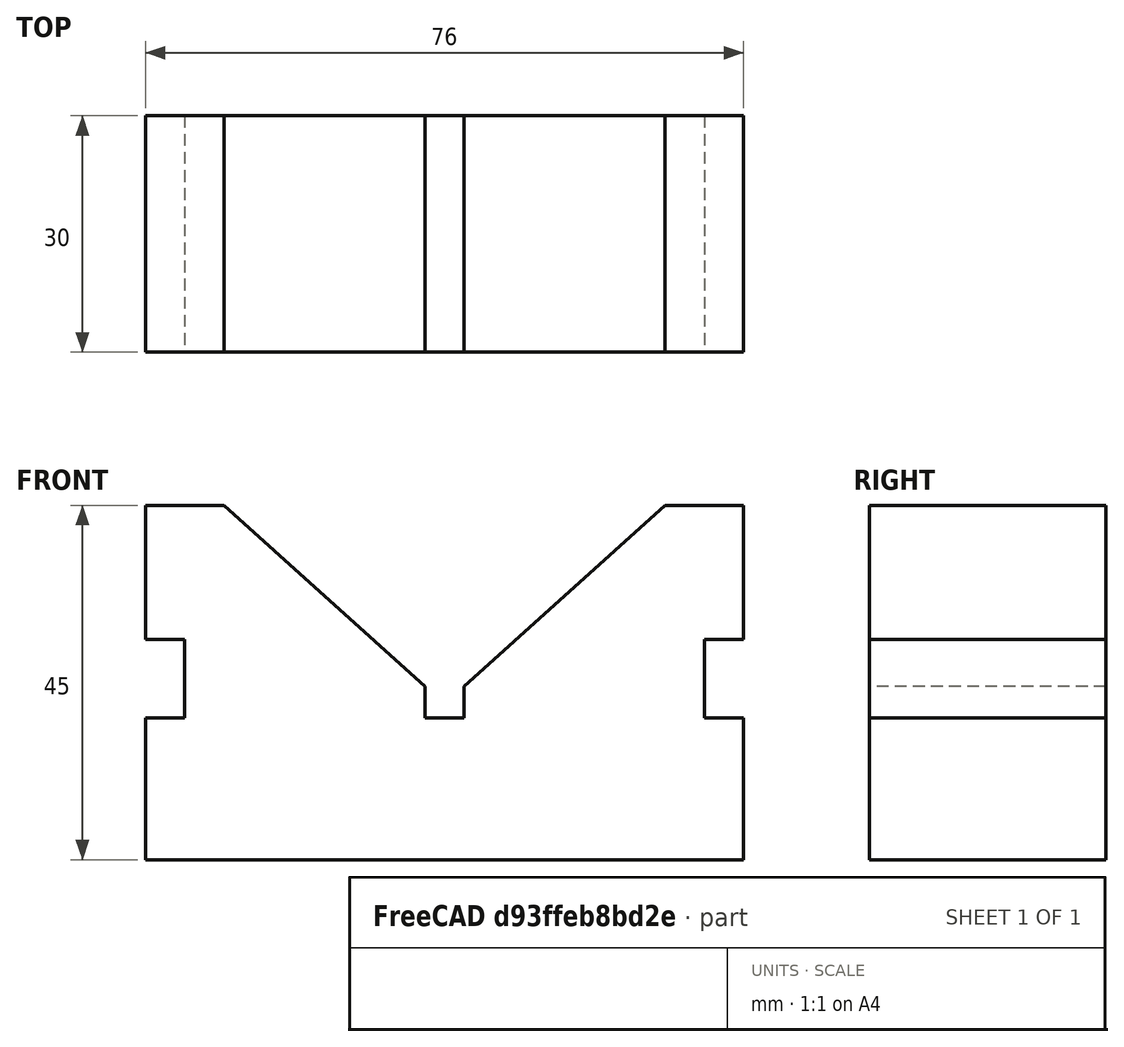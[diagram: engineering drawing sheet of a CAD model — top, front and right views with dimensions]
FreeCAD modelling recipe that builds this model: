
FCSTD DOCUMENT  (FreeCAD 0.18R4 (GitTag))
Label: Assignment-1
License: All rights reserved
LicenseURL: http://en.wikipedia.org/wiki/All_rights_reserved
objects: TechDraw::DrawViewDimension×9, TechDraw::DrawViewAnnotation×4, TechDraw::DrawViewPart×3, Sketcher::SketchObject×1, PartDesign::Pad×1, PartDesign::Body×1, TechDraw::DrawSVGTemplate×1, TechDraw::DrawPage×1
note: 4 computed .brp shape members not serialized (recipe doc carries the construction recipe); baked Part::Feature solids carry a one-line shape summary decoded from their .brp

FEATURE [Sketcher::SketchObject] Sketch
  MapMode = 5
  Placement = pos=(0,0,0) rot=(1,0,0;1.5708rad)
  Support = -> [XZ_Plane]
  sketch-geometry (20):
    g0: LineSegment StartX=0 StartY=0 StartZ=0 EndX=-38 EndY=0 EndZ=0
    g1: LineSegment StartX=-38 StartY=18 StartZ=0 EndX=-38 EndY=0 EndZ=0
    g2: LineSegment StartX=-38 StartY=18 StartZ=0 EndX=-33 EndY=18 EndZ=0
    g3: LineSegment StartX=-33 StartY=28 StartZ=0 EndX=-33 EndY=18 EndZ=0
    g4: LineSegment StartX=-38 StartY=28 StartZ=0 EndX=-33 EndY=28 EndZ=0
    g5: LineSegment StartX=-38 StartY=45 StartZ=0 EndX=-38 EndY=28 EndZ=0
    g6: LineSegment StartX=-38 StartY=45 StartZ=0 EndX=-28 EndY=45 EndZ=0
    g7: LineSegment StartX=-28 StartY=45 StartZ=0 EndX=-2.5 EndY=22 EndZ=0
    g8: LineSegment StartX=-2.5 StartY=22 StartZ=0 EndX=-2.5 EndY=18 EndZ=0
    g9: LineSegment StartX=-2.5 StartY=18 StartZ=0 EndX=0 EndY=18 EndZ=0
    g10: LineSegment StartX=0 StartY=0 StartZ=0 EndX=38 EndY=0 EndZ=0
    g11: LineSegment StartX=38 StartY=18 StartZ=0 EndX=38 EndY=0 EndZ=0
    g12: LineSegment StartX=38 StartY=18 StartZ=0 EndX=33 EndY=18 EndZ=0
    g13: LineSegment StartX=33 StartY=28 StartZ=0 EndX=33 EndY=18 EndZ=0
    g14: LineSegment StartX=38 StartY=28 StartZ=0 EndX=33 EndY=28 EndZ=0
    g15: LineSegment StartX=38 StartY=45 StartZ=0 EndX=38 EndY=28 EndZ=0
    g16: LineSegment StartX=38 StartY=45 StartZ=0 EndX=28 EndY=45 EndZ=0
    g17: LineSegment StartX=28 StartY=45 StartZ=0 EndX=2.5 EndY=22 EndZ=0
    g18: LineSegment StartX=2.5 StartY=22 StartZ=0 EndX=2.5 EndY=18 EndZ=0
    g19: LineSegment StartX=2.5 StartY=18 StartZ=0 EndX=0 EndY=18 EndZ=0
  constraints (56):
    c: Coincident(g0,g-1)
    c: Parallel(g0,g-1)
    c: DistanceX(g0,g0) = 38
    c: Coincident(g1,g0)
    c: Parallel(g1,g-2)
    c: DistanceY(g1,g1) = 18
    c: Coincident(g2,g1)
    c: Parallel(g2,g-1)
    c: DistanceX(g2,g2) = 5
    c: Coincident(g3,g2)
    c: Parallel(g3,g-2)
    c: DistanceY(g3,g3) = 10
    c: Coincident(g3,g4)
    c: Parallel(g-1,g4)
    c: DistanceX(g4,g4) = 5
    c: Coincident(g5,g4)
    c: Parallel(g5,g-2)
    c: DistanceY(g5,g5) = 17
    c: Coincident(g6,g5)
    c: Parallel(g6,g-1)
    c: DistanceX(g6,g6) = 10
    c: DistanceY(g0,g7) = 22
    c: Coincident(g7,g6)
    c: Coincident(g8,g7)
    c: Parallel(g8,g-2)
    c: DistanceY(g8,g8) = 4
    c: Coincident(g9,g8)
    c: Parallel(g9,g0)
    c: DistanceX(g9,g9) = 2.5
    c: Coincident(g11,g10)
    c: Coincident(g12,g11)
    c: Coincident(g13,g12)
    c: Coincident(g13,g14)
    c: Coincident(g15,g14)
    c: Coincident(g16,g15)
    c: Coincident(g17,g16)
    c: Coincident(g18,g17)
    c: Coincident(g19,g18)
    c: Parallel(g19,g10)
    c: Equal(g7,g17)
    c: Equal(g16,g6)
    c: Equal(g15,g5)
    c: Equal(g9,g19)
    c: Equal(g8,g18)
    c: Equal(g5,g15)
    c: Equal(g4,g14)
    c: Equal(g3,g13)
    c: Equal(g2,g12)
    c: Equal(g1,g11)
    c: Equal(g0,g10)
    c: Equal(g1,g11)
    c: Equal(g16,g6)
    c: Equal(g18,g8)
    c: Equal(g6,g16)
    c: Equal(g6,g16)
    c: Equal(g9,g19)
FEATURE [PartDesign::Pad] Pad
  Length = 30
  Length2 = 100
  Placement = pos=(0,0,0) rot=(1,0,0;1.5708rad)
  Profile = -> Sketch
  Type = 0
FEATURE [PartDesign::Body] Body
  Group = -> [Sketch,Pad]
  Origin = -> Origin
  Tip = -> Pad
FEATURE [TechDraw::DrawSVGTemplate] Template
  EditableTexts = Designed_by_Name=SOUMOJIT SHOME; Drawing_number=Drawing number - 02; FC-Date=08/11/2022; FC-SC=1:1; FC-SH=02; FC-Title=Academy of Technology; Subtitle=ECE-3 (X) ROLL- 139; Weight=Weight
  Height = 210
  Orientation = 1
  Width = 297
FEATURE [TechDraw::DrawViewPart] View
  CoarseView = false
  Direction = (0,-1,0)
  Focus = 100
  HardHidden = false
  IsoCount = 0
  IsoHidden = false
  IsoVisible = false
  LockPosition = false
  Perspective = false
  Rotation = 0
  ScaleType = 0
  SeamHidden = false
  SeamVisible = false
  SmoothHidden = false
  SmoothVisible = false
  Source = -> [Pad]
  X = 81.9468
  Y = 154.318
FEATURE [TechDraw::DrawViewPart] View001
  CoarseView = false
  Direction = (0,0,1)
  Focus = 100
  HardHidden = false
  IsoCount = 0
  IsoHidden = false
  IsoVisible = false
  LockPosition = false
  Perspective = false
  Rotation = 0
  ScaleType = 0
  SeamHidden = false
  SeamVisible = false
  SmoothHidden = false
  SmoothVisible = false
  Source = -> [Pad]
  X = 79.6067
  Y = 63.498
FEATURE [TechDraw::DrawViewPart] View002
  CoarseView = false
  Direction = (0.577,-0.577,0.577)
  Focus = 100
  HardHidden = false
  IsoCount = 0
  IsoHidden = false
  IsoVisible = false
  LockPosition = false
  Perspective = false
  Rotation = 0
  ScaleType = 0
  SeamHidden = false
  SeamVisible = false
  SmoothHidden = false
  SmoothVisible = false
  Source = -> [Pad]
  X = 215.733
  Y = 138.202
FEATURE [TechDraw::DrawViewDimension] Dimension
  Arbitrary = false
  FormatSpec = %.2f
  LockPosition = false
  MeasureType = 1
  OverTolerance = 0
  References2D = -> [View]
  Rotation = 0
  ScaleType = 0
  Type = 1
  UnderTolerance = 0
  X = -37.1162
  Y = 35.9027
FEATURE [TechDraw::DrawViewDimension] Dimension001
  Arbitrary = false
  FormatSpec = %.2f
  LockPosition = false
  MeasureType = 1
  OverTolerance = 0
  References2D = -> [View]
  Rotation = 0
  ScaleType = 0
  Type = 2
  UnderTolerance = 0
  X = 50.4704
  Y = 6.63661
FEATURE [TechDraw::DrawViewDimension] Dimension002
  Arbitrary = false
  FormatSpec = %.2f
  LockPosition = false
  MeasureType = 1
  OverTolerance = 0
  References2D = -> [View]
  Rotation = 0
  ScaleType = 0
  Type = 1
  UnderTolerance = 0
  X = 12.5602
  Y = -40.9168
FEATURE [TechDraw::DrawViewDimension] Dimension003
  Arbitrary = false
  FormatSpec = %.2f
  LockPosition = false
  MeasureType = 1
  OverTolerance = 0
  References2D = -> [View]
  Rotation = 0
  ScaleType = 0
  Type = 2
  UnderTolerance = 0
  X = -59.0003
  Y = 10.7875
FEATURE [TechDraw::DrawViewDimension] Dimension004
  Arbitrary = false
  FormatSpec = %.2f
  LockPosition = false
  MeasureType = 1
  OverTolerance = 0
  References2D = -> [View]
  Rotation = 0
  ScaleType = 0
  Type = 2
  UnderTolerance = 0
  X = -66.4537
  Y = -19.373
FEATURE [TechDraw::DrawViewDimension] Dimension005
  Arbitrary = false
  FormatSpec = %.2f
  LockPosition = false
  MeasureType = 1
  OverTolerance = 0
  References2D = -> [View001]
  Rotation = 0
  ScaleType = 0
  Type = 2
  UnderTolerance = 0
  X = 51.9004
  Y = 5.42978
FEATURE [TechDraw::DrawViewDimension] Dimension006
  Arbitrary = false
  FormatSpec = %.2f
  LockPosition = false
  MeasureType = 1
  OverTolerance = 0
  References2D = -> [View]
  Rotation = 0
  ScaleType = 0
  Type = 2
  UnderTolerance = 0
  X = 9.18176
  Y = 26.9807
FEATURE [TechDraw::DrawViewDimension] Dimension007
  Arbitrary = false
  FormatSpec = %.2f
  LockPosition = false
  MeasureType = 1
  OverTolerance = 0
  References2D = -> [View]
  Rotation = 0
  ScaleType = 0
  Type = 1
  UnderTolerance = 0
  X = -24.0065
  Y = -29.8891
FEATURE [TechDraw::DrawViewDimension] Dimension008
  Arbitrary = false
  FormatSpec = %.2f
  LockPosition = false
  MeasureType = 1
  OverTolerance = 0
  References2D = -> [View]
  Rotation = 0
  ScaleType = 0
  Type = 1
  UnderTolerance = 0
  X = -7.80517
  Y = 25.714
FEATURE [TechDraw::DrawViewAnnotation] Annotation
  Font = osifont
  LineSpace = 80
  LockPosition = false
  MaxWidth = -1
  Rotation = 0
  ScaleType = 0
  Text = Front View
  TextSize = 5
  TextStyle = 0
  X = 79.4432
  Y = 100.619
FEATURE [TechDraw::DrawViewAnnotation] Annotation001
  Font = osifont
  LineSpace = 80
  LockPosition = false
  MaxWidth = -1
  Rotation = 0
  ScaleType = 0
  Text = Top View
  TextSize = 5
  TextStyle = 0
  X = 79.0418
  Y = 34.1008
FEATURE [TechDraw::DrawViewAnnotation] Annotation002
  Font = osifont
  LineSpace = 80
  LockPosition = false
  MaxWidth = -1
  Rotation = 0
  ScaleType = 0
  Text = Isometric View
  TextSize = 5
  TextStyle = 0
  X = 203.252
  Y = 86.2075
FEATURE [TechDraw::DrawViewAnnotation] Annotation003
  Font = osifont
  LineSpace = 80
  LockPosition = false
  MaxWidth = -1
  Rotation = 0
  ScaleType = 0
  Text =  V Block
  TextSize = 5
  TextStyle = 0
  X = 203.435
  Y = 35.2267
FEATURE [TechDraw::DrawPage] Page
  KeepUpdated = true
  ProjectionType = 0
  Template = -> Template
  Views = -> [View,View001,View002,Dimension,Dimension001,Dimension002,Dimension003,Dimension004,Dimension005,Dimension006,Dimension007,Dimension008,Annotation,Annotation001,Annotation002,Annotation003]
